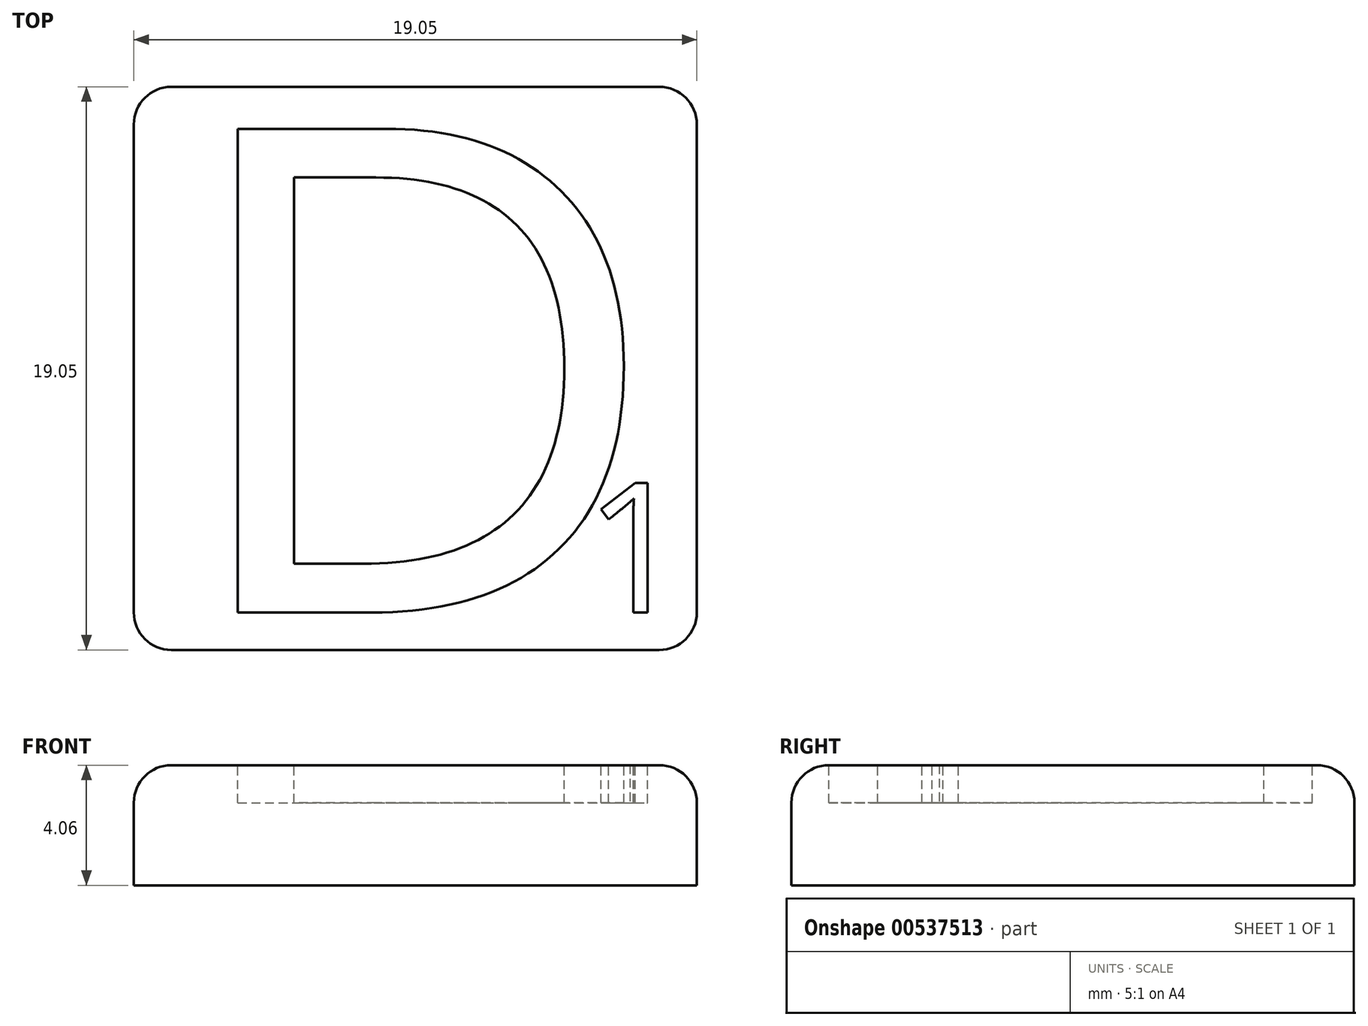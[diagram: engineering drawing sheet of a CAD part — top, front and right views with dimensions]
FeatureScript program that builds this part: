
annotation { "Feature Type Name" : "Feature", "Feature Type Description" : "" }
export const myFeature = defineFeature(function(context is Context, id is Id, definition is map)
    precondition{}
    {
        {
            var Q0;
            Q0=qCreatedBy(makeId("Top.planeOp"),FACE);
            var sketch = newSketch(context, id + "F0", { "sketchPlane" : qUnion([Q0])});
            skLineSegment(sketch, "E0.bottom", {"start": v(0, 0) * mm, "end": v(19.05, 0) * mm});
            skLineSegment(sketch, "E0.top", {"start": v(0, 19.05) * mm, "end": v(19.05, 19.05) * mm});
            skLineSegment(sketch, "E0.left", {"start": v(0, 0) * mm, "end": v(0, 19.05) * mm});
            skLineSegment(sketch, "E0.right", {"start": v(19.05, 0) * mm, "end": v(19.05, 19.05) * mm});
            skSolve(sketch);
        }
        {
            var Q0;
            Q0=makeQuery(id+"F0.imprint","IMPRINT",FACE,{"disambiguationData":[TD([[makeQuery(id+"F0.imprint","IMPRINT",EDGE,{"derivedFrom":sQuery(id+"F0.wireOp",EDGE,"E0.bottom")}),1.0]])]});
            extrude(context, id + "F1", {"entities" : qUnion([Q0]), "depth" : 4.06 * mm});
        }
        {
            var Q0;
            Q0=makeQuery(id+"F1.opExtrude","SWEPT_EDGE",EDGE,{"disambiguationData":[OSD([sQuery(id+"F0.wireOp",EDGE,"E0.bottom"),sQuery(id+"F0.wireOp",EDGE,"E0.right")])]});
            var Q1;
            Q1=makeQuery(id+"F1.opExtrude","CAP_EDGE",EDGE,{"disambiguationData":[OSD([sQuery(id+"F0.wireOp",EDGE,"E0.right")])],"isStart":false});
            var Q2;
            Q2=makeQuery(id+"F1.opExtrude","CAP_EDGE",EDGE,{"disambiguationData":[OSD([sQuery(id+"F0.wireOp",EDGE,"E0.bottom")])],"isStart":false});
            var Q3;
            Q3=makeQuery(id+"F1.opExtrude","SWEPT_EDGE",EDGE,{"disambiguationData":[OSD([sQuery(id+"F0.wireOp",EDGE,"E0.bottom"),sQuery(id+"F0.wireOp",EDGE,"E0.left")])]});
            var Q4;
            Q4=makeQuery(id+"F1.opExtrude","CAP_EDGE",EDGE,{"disambiguationData":[OSD([sQuery(id+"F0.wireOp",EDGE,"E0.left")])],"isStart":false});
            var Q5;
            Q5=makeQuery(id+"F1.opExtrude","SWEPT_EDGE",EDGE,{"disambiguationData":[OSD([sQuery(id+"F0.wireOp",EDGE,"E0.top"),sQuery(id+"F0.wireOp",EDGE,"E0.right")])]});
            var Q6;
            Q6=makeQuery(id+"F1.opExtrude","CAP_EDGE",EDGE,{"disambiguationData":[OSD([sQuery(id+"F0.wireOp",EDGE,"E0.top")])],"isStart":false});
            var Q7;
            Q7=makeQuery(id+"F1.opExtrude","SWEPT_EDGE",EDGE,{"disambiguationData":[OSD([sQuery(id+"F0.wireOp",EDGE,"E0.top"),sQuery(id+"F0.wireOp",EDGE,"E0.left")])]});
            fillet(context, id + "F2", {"entities" : qUnion([Q0, Q1, Q2, Q3, Q4, Q5, Q6, Q7]), "radius" : 1.27 * mm, "tangentPropagation" : true, "allowEdgeOverflow" : false});
        }
        {
            var Q0;
            Q0=makeQuery(id+"F1.opExtrude","CAP_FACE",FACE,{"disambiguationData":[OSD([sQuery(id+"F0.wireOp",EDGE,"E0.bottom"),sQuery(id+"F0.wireOp",EDGE,"E0.top"),sQuery(id+"F0.wireOp",EDGE,"E0.left"),sQuery(id+"F0.wireOp",EDGE,"E0.right")])],"isStart":false});
            var sketch = newSketch(context, id + "F3", { "sketchPlane" : qUnion([Q0])});
            skText(sketch, "E1", { "text": "D", "fontName": "OpenSans-Regular.ttf"});
            const initialGuessF3  = {"E1": [0.00127, 0.00127, 1, 0, 0.0165]};
            skSetInitialGuess(sketch, initialGuessF3);
            skSolve(sketch);
        }
        {
            var Q0;
            Q0 = qSketchRegion(id + "F3", true);
            extrude(context, id + "F4", {"entities" : qUnion([Q0]), "operationType" : NewBodyOperationType.REMOVE, "oppositeDirection" : true, "depth" : 1.27 * mm, "offsetDistance" : 25.4 * mm});
        }
        {
            var Q0;
            {var subQ0=sQuery(id+"F0.wireOp",EDGE,"E0.top");var subQ1=sQuery(id+"F0.wireOp",EDGE,"E0.bottom");var subQ2=sQuery(id+"F0.wireOp",EDGE,"E0.right");Q0=makeQuery(id+"F4.boolean.opBoolean","SPLIT",FACE,{"disambiguationData":[TD([makeQuery(id+"F2.opFillet","BLEND_FACE",FACE,{"disambiguationData":[OSD([subQ2])]})])],"derivedFrom":makeQuery(id+"F1.opExtrude","CAP_FACE",FACE,{"disambiguationData":[OSD([subQ1,subQ0,sQuery(id+"F0.wireOp",EDGE,"E0.left"),subQ2])],"isStart":false})});}
            var sketch = newSketch(context, id + "F5", { "sketchPlane" : qUnion([Q0])});
            skText(sketch, "E2", { "text": "1\n", "fontName": "OpenSans-Regular.ttf"});
            const initialGuessF5  = {"E2": [0.01524, 0.00127, 1, 0, 0.00442]};
            skSetInitialGuess(sketch, initialGuessF5);
            skSolve(sketch);
        }
        {
            var Q0;
            Q0 = qSketchRegion(id + "F5", true);
            extrude(context, id + "F6", {"entities" : qUnion([Q0]), "operationType" : NewBodyOperationType.REMOVE, "oppositeDirection" : true, "depth" : 1.27 * mm, "offsetDistance" : 25.4 * mm});
        }
    });
